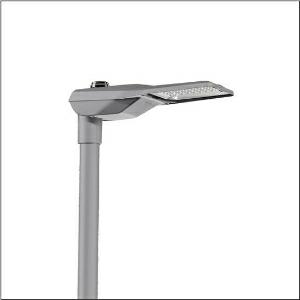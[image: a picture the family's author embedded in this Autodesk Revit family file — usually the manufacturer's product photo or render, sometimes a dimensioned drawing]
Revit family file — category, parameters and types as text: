
# Revit family: streetlight_sl_21_mini___stw1_0a_5xe6e37n08jb_6c36
name_source: partatom
category: Lighting Fixtures
units: mm (PartAtom-declared; Revit-internal decimal feet)

## family parameters
Cut with Voids When Loaded = No
Host = Face
Light Source = No
Part Type = Normal
Room Calculation Point = No
Round Connector Dimension = Use Diameter
Shared = No

## types (1)
- --- (1 x LED, 12830 lm, 87.3 W, 3000K)
    Apparent Load = 87 VA
    CIE Flux Codes = 39 75 98 100 100
    Color Rendering = 70
    Color Temperature = 3000K
    Default Elevation = 1800 mm
    Description = Streetlight SL 21 mini, mast luminaire, primary light control with lens, of PMMA, primary optical cover: cover, of toughened safety glass, transparent, light distribution: STW1.0a, light emission: direct distribution, primary light characteristic: asymmetric, installation type: side-entry, LED, 3G 2.5mm², High Power LED, rated luminous flux: 12.830lm, luminous efficacy: 147lm/W, light colour: 730, colour temperature: 3000K, control gear: NEMA (7pin), control: overheat protection, pre-setting: linear dimming characteristic, constant luminous flux control, time-dependent luminous flux control, flexible luminous flux parameterisation, mains connection: 230..240V, AC, 50/60Hz, connection cable pre-assembled, cable length: 10,5m, wiring characteristics: H05VV-F, start of lifetime: 87W, end of service life: 90W, reduction: 40W, luminaire housing, of diecast aluminium (EN AC-44300), powder-coated, Siteco® metallic grey (DB 702S), corrosivity category C5 mid according to DIN EN ISO 12944, multi-level sealing system, sealing non-destructively replaceable, inclination adjustable: 0°, 5°, 10°, 15°, length: 628mm, width: 235mm, height: 110mm, spigot size: 42mm (side-entry), mounting height: 4..8m, protection rating (complete): IP66, insulation class (complete): insulation class I (protective earthing), certification: CE, ENEC, ENEC+, VDE, impact resistance: IK10, permissible operating ambient temperature for outdoor applications: -40..+50°C, standard-compliant lighting for roads and squares, packaging unit: 1 piece

Light Distribution: STW1.0a
    Height = 110 mm
    Lamp = 1 x LED
    Lamp Light Flux = 12830 lm
    Lamp Power = 87.3 W
    Lamp count = 1
    Length = 625 mm
    Luminous efficacy = 147 lm/W
    Manufacturer = Siteco
    ModVariant = No
    Model = 5XE6E37N08JB
    Number of Poles = 1
    OnlyDefault = Yes
    Power Factor = 1
    Product Name = Streetlight SL 21 mini | STW1.0a
    Product group = mast luminaire | pylon top
    ProductGroupID = 6100
    Protection Class = Protection class I
    Protection Degree = IP 66
    RLX_Detail_Level = 1
    RLX_Emergency_Light_Flux = 0 lm
    RLX_Emergency_Type = 0
    RLX_Emergency_Type_DB = No
    RlxData = <blob elided: 26093 chars, md5=bb4da22d>
    Socket = socket
    Standby Power = 0 W
    System Light Flux = 12830 lm
    System Power = 87 W
    Type Comments = factory setting: luminous flux: 100 % | dim-lin: 254 | 915 mA
    Type Image = l_1294379.jpg
    URL = http://relux.com
    VarID = @adj_135012
    Voltage = 0 V
    Weight = 0.00 kg
    Width = 234 mm

## geometry (parser evidence)
native form markers: Blend x4, Sweep x13
no freeform markers — native parametric forms only
